# Revit family: Faucet-Lavatory-Spout-KOHLER-COMPONENTS-K-77969BR_1
name_source: partatom
category: Plumbing Fixtures
revit_build: Autodesk Revit 2017 (Build: 20160225_1515(x64)
units: mm (PartAtom-declared; Revit-internal decimal feet)

## family parameters
Cut with Voids When Loaded = No
Host = Face
OmniClass Number = 23.31.11.00
OmniClass Title = Faucets
Part Type = Normal
Room Calculation Point = No
Round Connector Dimension = Use Diameter
Shared = No

## types (4) — shared parameters
ADA Compliant = No
Assembly Code = D2010
CW Connection = Yes
Cold Water Inlet = Cold Water Inlet
Date Modified = 09/14/2021
Default Elevation = 36"
Description = Row spout for washbasin mixer
Drain Included = Yes
Flow Rate = 1 GPM
HW Connection = Yes
Height = 8 1/4"
Hot Water Inlet = Hot Water Inlet
Length = 6 5/8"
Manufacturer = KOHLER Co.
Master Format 2014 = 22 41 39
Master Format 2014 Name = Residential Faucets, Supplies, and Trim
Material = Premium Metal Construction
Pressure = 60.00 psi
Product Name = COMPONENTS
Product Page URL = https://br.kohler.com
Spout Reach = 6 5/8"
URL = https://br.kohler.com
Vent Connection = No
Waste Connection = No
Waste Water Outlet = Waste Water Outlet
WaterSense Certified = No
Width = 2 3/8"

## per-type parameters (varying)
| type | Finish | Model | Type |
| BL-Matte Black | Kohler-Metal-BL-Matte_Black | K-77969BR-BL | 4 |
| CP-Polished Chrome | Kohler-Metal-CP-Polished_Chrome | K-77969BR-CP | 1 |
| BN-Vibrant Brushed Nickel | Kohler-Metal-BN-Vibrant_Brushed_Nickel | K-77969BR-BN | 2 |
| RGD-Polished Rose Gold | Kohler-Metal-RGD-Polished_Rose_Gold | K-77969BR-RGD | 3 |

## geometry (parser evidence)
native form markers: Sweep x6
no freeform markers — native parametric forms only
